# Revit family: In-Line-Centrifugal-Duct-Fan_VIBK_Carnes
name_source: partatom
category: Mechanical Equipment
revit_build: Autodesk Revit Architecture 2012 (Build: 20110916_2132(x64)
units: mm (PartAtom-declared; Revit-internal decimal feet)

## types (11) — shared parameters
04 CSI = 23 34 23
95 CSI = 15830
Assembly Code = D3040200
Catalog URL = http://www.carnes.com
Default Elevation = 0"
Description = Centrifugal Duct Fan
Housing = Aluminum-Carnes-Spun-Brushed
IOM Instructions URL = http://www.carnes.com
Manufacturer = Carnes Company
Manufacturer Fax = 608-845-6470
Product Page URL = http://www.carnes.com
URL = http://www.carnes.com
Warranty URL = http://www.carnes.com
ecoScorecard Product Page = http://ecoscorecard.com

## per-type parameters (varying)
| type | A | B | C | D | Damper Size | E | F | G | Radius |
| VIBK 06 | 14" | 28 5/8" | 12" | 16 1/2" | 12" | 25 1/8" | 12 1/2" | 12" | 6" |
| VIBK 08 | 14" | 28 5/8" | 12" | 16 1/2" | 12" | 25 1/8" | 12 1/2" | 12" | 6" |
| VIBK 10 | 18" | 32 1/8" | 16" | 20 1/2" | 16" | 28 5/8" | 16 1/2" | 12" | 8" |
| VIBK 12 | 18" | 32 1/8" | 16" | 20 1/2" | 16" | 28 5/8" | 16 1/2" | 12" | 8" |
| VIBK 15 | 24" | 34 7/8" | 22" | 26 1/2" | 22" | 31 3/8" | 22 1/2" | 12" | 11" |
| VIBK 18 | 28" | 36 1/8" | 26" | 30 1/2" | 26" | 32 5/8" | 26 1/2" | 12" | 13" |
| VIBK 21 | 31" | 39 3/8" | 29" | 33" | 29" | 33 7/8" | 27 1/2" | 14" | 14 1/2" |
| VIBK 24 | 40" | 42 5/8" | 38" | 42" | 38" | 37 1/8" | 36 1/2" | 14" | 19" |
| VIBK 30 | 48" | 46 1/8" | 46" | 50" | 46" | 40 5/8" | 44 1/2" | 14" | 23" |
| VIBK 36 | 56" | 48 7/8" | 54" | 58" | 54" | 43 3/8" | 55 1/2" | 14" | 27" |
| VIBK 42 | 56" | 50 7/8" | 54" | 58" | 54" | 43 3/8" | 55 1/2" | 15" | 27" |

note: column(s) folded — value = type name in every type: Model

## geometry (parser evidence)
native form markers: Blend x2, Sweep x5
no freeform markers — native parametric forms only
